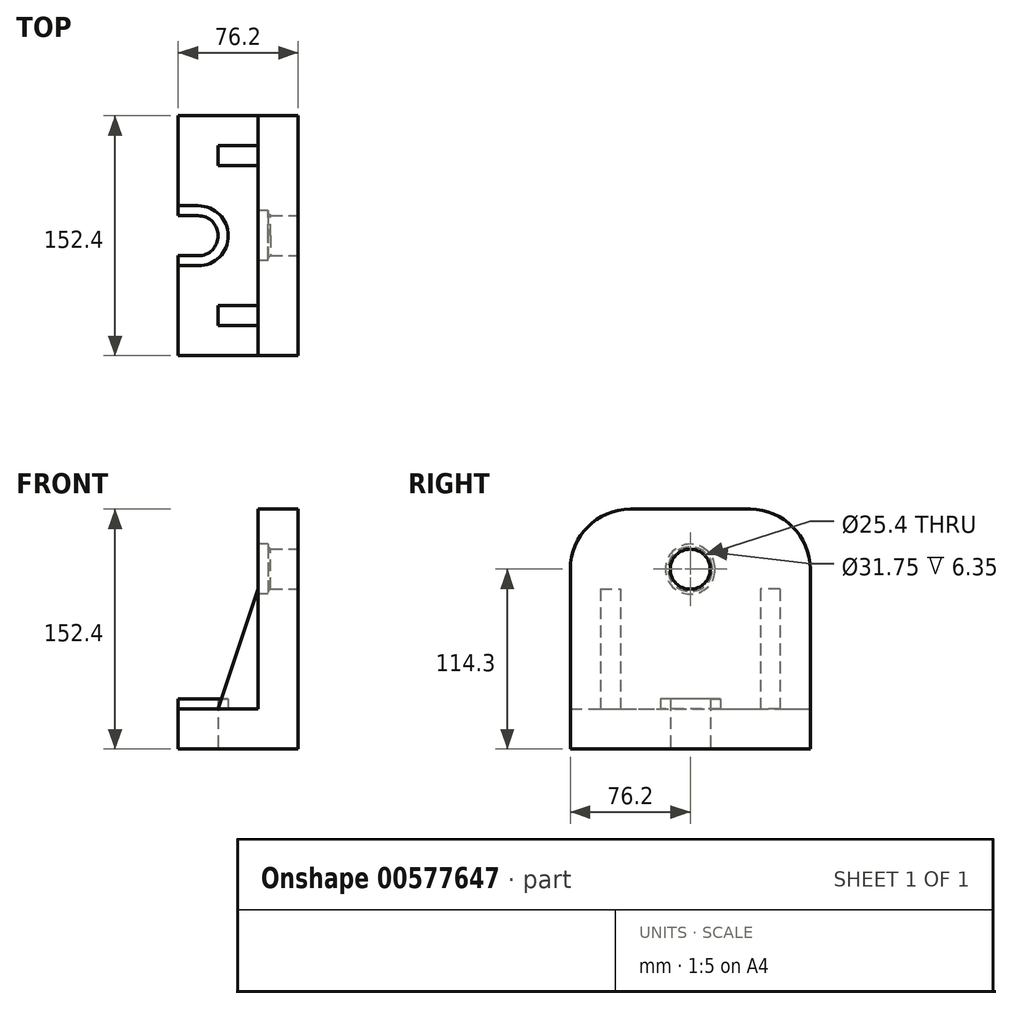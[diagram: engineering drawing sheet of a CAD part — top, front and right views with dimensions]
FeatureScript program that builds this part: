
annotation { "Feature Type Name" : "Feature", "Feature Type Description" : "" }
export const myFeature = defineFeature(function(context is Context, id is Id, definition is map)
    precondition{}
    {
        {
            var Q0;
            Q0=qCreatedBy(makeId("Front.planeOp"),FACE);
            var sketch = newSketch(context, id + "F0", { "sketchPlane" : qUnion([Q0])});
            skLineSegment(sketch, "E0", {"start": v(0, 152.4) * mm, "end": v(-25.4, 152.4) * mm});
            skLineSegment(sketch, "E1", {"start": v(-25.4, 25.4) * mm, "end": v(-76.2, 25.4) * mm});
            skLineSegment(sketch, "E2", {"start": v(-76.2, 25.4) * mm, "end": v(-76.2, 0) * mm});
            skLineSegment(sketch, "E3", {"start": v(-76.2, 0) * mm, "end": v(0, 0) * mm});
            skLineSegment(sketch, "E4", {"start": v(0, 0) * mm, "end": v(0, 152.4) * mm});
            skLineSegment(sketch, "E5", {"start": v(-25.4, 152.4) * mm, "end": v(-25.4, 25.4) * mm});
            skSolve(sketch);
        }
        {
            var Q0;
            Q0=makeQuery(id+"F0.imprint","IMPRINT",FACE,{"disambiguationData":[TD([[makeQuery(id+"F0.imprint","IMPRINT",EDGE,{"derivedFrom":sQuery(id+"F0.wireOp",EDGE,"E0")}),1.0]])]});
            extrude(context, id + "F1", {"entities" : qUnion([Q0]), "endBound" : BoundingType.SYMMETRIC, "depth" : 152.4 * mm, "offsetDistance" : 25.4 * mm});
        }
        {
            var Q0;
            Q0=makeQuery(id+"F1.opExtrude","SWEPT_FACE",FACE,{"disambiguationData":[OSD([sQuery(id+"F0.wireOp",EDGE,"E4")])]});
            var sketch = newSketch(context, id + "F2", { "sketchPlane" : qUnion([Q0])});
            skCircle(sketch, "E6", {"center": v(0, 114.3) * mm, "radius": 12.7 * mm});
            skSolve(sketch);
        }
        {
            var Q0;
            Q0=makeQuery(id+"F2.imprint","IMPRINT",FACE,{"disambiguationData":[TD([[makeQuery(id+"F2.imprint","IMPRINT",EDGE,{"derivedFrom":sQuery(id+"F2.wireOp",EDGE,"E6")}),1.0]])]});
            extrude(context, id + "F3", {"entities" : qUnion([Q0]), "operationType" : NewBodyOperationType.REMOVE, "endBound" : BoundingType.THROUGH_ALL, "oppositeDirection" : true, "depth" : 25.4 * mm, "offsetDistance" : 25.4 * mm});
        }
        {
            var Q0;
            Q0=makeQuery(id+"F1.opExtrude","SWEPT_FACE",FACE,{"disambiguationData":[OSD([sQuery(id+"F0.wireOp",EDGE,"E3")])]});
            var sketch = newSketch(context, id + "F4", { "sketchPlane" : qUnion([Q0])});
            skLineSegment(sketch, "E7", {"start": v(-76.2, 12.7) * mm, "end": v(-63.5, 12.7) * mm});
            skLineSegment(sketch, "E8", {"start": v(-76.2, -12.7) * mm, "end": v(-63.5, -12.7) * mm});
            skArc(sketch, "E9", {"start": v(-63.5, -12.7) * mm, "mid": v(-50.8, 0) * mm, "end": v(-63.5, 12.7) * mm});
            skSolve(sketch);
        }
        {
            var Q0;
            Q0 = qSketchRegion(id + "F4", true);
            var Q1;
            {var subQ0=sQuery(id+"F4.wireOp",EDGE,"E7");Q1=makeQuery(id+"F4.imprint","IMPRINT",FACE,{"disambiguationData":[TD([[makeQuery(id+"F4.imprint","IMPRINT",EDGE,{"derivedFrom":subQ0}),-1.0]])]});}
            extrude(context, id + "F5", {"entities" : qUnion([Q0, Q1]), "operationType" : NewBodyOperationType.REMOVE, "endBound" : BoundingType.THROUGH_ALL, "oppositeDirection" : true, "depth" : 25.4 * mm, "offsetDistance" : 25.4 * mm});
        }
        {
            var Q0;
            Q0=makeQuery(id+"F1.opExtrude","SWEPT_FACE",FACE,{"disambiguationData":[OSD([sQuery(id+"F0.wireOp",EDGE,"E5")])]});
            var sketch = newSketch(context, id + "F6", { "sketchPlane" : qUnion([Q0])});
            skCircle(sketch, "E10", {"center": v(0, 114.3) * mm, "radius": 15.88 * mm});
            skSolve(sketch);
        }
        {
            var Q0;
            Q0 = qSketchRegion(id + "F6", true);
            extrude(context, id + "F7", {"entities" : qUnion([Q0]), "operationType" : NewBodyOperationType.REMOVE, "oppositeDirection" : true, "depth" : 6.35 * mm, "offsetDistance" : 25.4 * mm});
        }
        {
            var Q0;
            Q0=makeQuery(id+"F1.opExtrude","CAP_EDGE",EDGE,{"disambiguationData":[OSD([sQuery(id+"F0.wireOp",EDGE,"E0")])],"isStart":false});
            var Q1;
            Q1=makeQuery(id+"F1.opExtrude","CAP_EDGE",EDGE,{"disambiguationData":[OSD([sQuery(id+"F0.wireOp",EDGE,"E0")])],"isStart":true});
            fillet(context, id + "F8", {"entities" : qUnion([Q0, Q1]), "radius" : 38.1 * mm, "tangentPropagation" : true, "allowEdgeOverflow" : false});
        }
        {
            var Q0;
            Q0=qCreatedBy(makeId("Front.planeOp"),FACE);
            var sketch = newSketch(context, id + "F9", { "sketchPlane" : qUnion([Q0])});
            skLineSegment(sketch, "E11.0", {"start": v(-25.4, 25.4) * mm, "end": v(-76.2, 25.4) * mm});
            skLineSegment(sketch, "E12.0", {"start": v(-25.4, 114.3) * mm, "end": v(-25.4, 25.4) * mm});
            skSolve(sketch);
        }
        {
            var Q0;
            Q0=qCreatedBy(makeId("Front.planeOp"),FACE);
            cPlane(context, id + "F10", {"entities" : qUnion([Q0]), "cplaneType" : CPlaneType.OFFSET, "offset" : 44.45 * mm, "width" : 152.4 * mm, "height" : 152.4 * mm});
        }
        {
            var Q0;
            Q0=qCreatedBy(id+"F10.planeOp",FACE);
            var sketch = newSketch(context, id + "F11", { "sketchPlane" : qUnion([Q0])});
            skLineSegment(sketch, "E13.0", {"start": v(-25.4, 101.6) * mm, "end": v(-25.4, 25.4) * mm});
            skLineSegment(sketch, "E14.0", {"start": v(-25.4, 25.4) * mm, "end": v(-50.8, 25.4) * mm});
            skPoint(sketch, "E15.orphan", {"position": v(-76.2, 25.4) * mm});
            skLineSegment(sketch, "E16", {"start": v(-25.4, 25.4) * mm, "end": v(-25.4, 101.6) * mm});
            skLineSegment(sketch, "E17", {"start": v(-25.4, 101.6) * mm, "end": v(-50.8, 25.4) * mm});
            skPoint(sketch, "E18.orphan", {"position": v(-25.4, 114.3) * mm});
            skSolve(sketch);
        }
        {
            var Q0;
            Q0=makeQuery(id+"F11.imprint","IMPRINT",FACE,{"disambiguationData":[TD([[makeQuery(id+"F11.imprint","IMPRINT",EDGE,{"derivedFrom":sQuery(id+"F11.wireOp",EDGE,"E14.0")}),-1.0]])]});
            extrude(context, id + "F12", {"entities" : qUnion([Q0]), "operationType" : NewBodyOperationType.ADD, "depth" : 12.7 * mm, "offsetDistance" : 25.4 * mm});
        }
        {
            var Q0;
            Q0=makeQuery(id+"F1.opExtrude","SWEPT_BODY",BODY,{"disambiguationData":[OSD([sQuery(id+"F0.wireOp",EDGE,"E0"),sQuery(id+"F0.wireOp",EDGE,"E1"),sQuery(id+"F0.wireOp",EDGE,"E2"),sQuery(id+"F0.wireOp",EDGE,"E3"),sQuery(id+"F0.wireOp",EDGE,"E4"),sQuery(id+"F0.wireOp",EDGE,"E5")])]});
            var Q1;
            Q1=qCreatedBy(makeId("Front.planeOp"),FACE);
            mirror(context, id + "F13", {"operationType" : NewBodyOperationType.ADD, "entities" : qUnion([Q0]), "mirrorPlane" : qUnion([Q1])});
        }
        {
            var Q0;
            Q0=makeQuery(id+"F7.boolean.opBoolean","COPY",EDGE,{"derivedFrom":makeQuery(id+"F7.opExtrude","CAP_EDGE",EDGE,{"disambiguationData":[OSD([sQuery(id+"F6.wireOp",EDGE,"E10")])],"isStart":true})});
            var Q1;
            Q1=makeQuery(id+"F7.boolean.opBoolean","INTERSECT",EDGE,{"derivedFrom":[makeQuery(id+"F3.boolean.opBoolean","COPY",FACE,{"derivedFrom":makeQuery(id+"F3.opExtrude","SWEPT_FACE",FACE,{"disambiguationData":[OSD([sQuery(id+"F2.wireOp",EDGE,"E6")])]})}),makeQuery(id+"F7.opExtrude","CAP_FACE",FACE,{"disambiguationData":[OSD([sQuery(id+"F6.wireOp",EDGE,"E10")])],"isStart":false})]});
            chamfer(context, id + "F14", {"entities" : qUnion([Q0, Q1]), "width" : 1.52 * mm, "tangentPropagation" : true});
        }
        {
            var Q0;
            {var subQ1=sQuery(id+"F0.wireOp",EDGE,"E2");Q0=makeQuery(id+"F5.boolean.opBoolean","SPLIT",FACE,{"disambiguationData":[TD([makeQuery(id+"F5.opExtrude","SWEPT_FACE",FACE,{"disambiguationData":[OSD([sQuery(id+"F4.wireOp",EDGE,"E8")])]})])],"derivedFrom":makeQuery(id+"F1.opExtrude","SWEPT_FACE",FACE,{"disambiguationData":[OSD([subQ1])]})});}
            var sketch = newSketch(context, id + "F15", { "sketchPlane" : qUnion([Q0])});
            skLineSegment(sketch, "E19.0", {"start": v(-12.7, 25.4) * mm, "end": v(-76.2, 25.4) * mm});
            skLineSegment(sketch, "E20", {"start": v(-12.7, 25.4) * mm, "end": v(-12.7, 31.75) * mm});
            skLineSegment(sketch, "E21", {"start": v(-12.7, 31.75) * mm, "end": v(-19.05, 31.75) * mm});
            skLineSegment(sketch, "E22", {"start": v(-19.05, 31.75) * mm, "end": v(-19.05, 25.4) * mm});
            skSolve(sketch);
        }
        {
            var Q0;
            {var subQ0=sQuery(id+"F15.wireOp",EDGE,"E20");Q0=makeQuery(id+"F15.imprint","IMPRINT",FACE,{"disambiguationData":[TD([[makeQuery(id+"F15.imprint","IMPRINT",EDGE,{"derivedFrom":subQ0}),1.0]])]});}
            var Q1;
            Q1=makeQuery(id+"F5.boolean.opBoolean","INTERSECT",EDGE,{"derivedFrom":[makeQuery(id+"F1.opExtrude","SWEPT_FACE",FACE,{"disambiguationData":[OSD([sQuery(id+"F0.wireOp",EDGE,"E1")])]}),makeQuery(id+"F5.opExtrude","SWEPT_FACE",FACE,{"disambiguationData":[OSD([sQuery(id+"F4.wireOp",EDGE,"E8")])]})]});
            var Q2;
            Q2=makeQuery(id+"F5.boolean.opBoolean","INTERSECT",EDGE,{"derivedFrom":[makeQuery(id+"F1.opExtrude","SWEPT_FACE",FACE,{"disambiguationData":[OSD([sQuery(id+"F0.wireOp",EDGE,"E1")])]}),makeQuery(id+"F5.opExtrude","SWEPT_FACE",FACE,{"disambiguationData":[OSD([sQuery(id+"F4.wireOp",EDGE,"E9")])]})]});
            var Q3;
            Q3=makeQuery(id+"F5.boolean.opBoolean","INTERSECT",EDGE,{"derivedFrom":[makeQuery(id+"F1.opExtrude","SWEPT_FACE",FACE,{"disambiguationData":[OSD([sQuery(id+"F0.wireOp",EDGE,"E1")])]}),makeQuery(id+"F5.opExtrude","SWEPT_FACE",FACE,{"disambiguationData":[OSD([sQuery(id+"F4.wireOp",EDGE,"E7")])]})]});
            sweep(context, id + "F16", {"operationType" : NewBodyOperationType.ADD, "profiles" : qUnion([Q0]), "path" : qUnion([Q1, Q2, Q3])});
        }
    });
